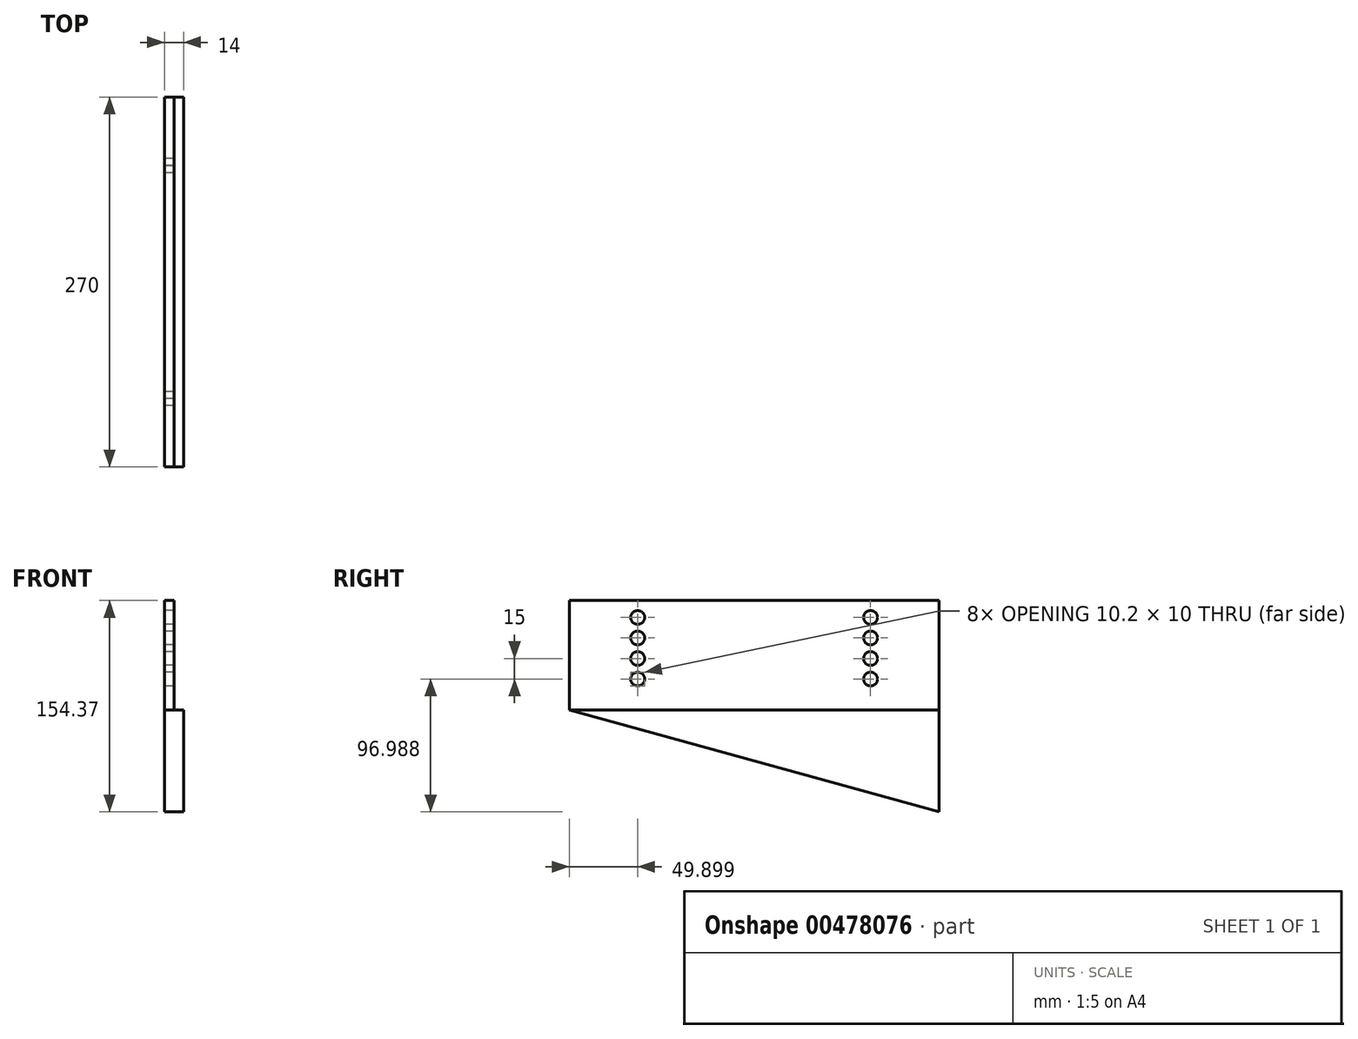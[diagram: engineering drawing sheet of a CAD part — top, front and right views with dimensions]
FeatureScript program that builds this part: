
annotation { "Feature Type Name" : "Feature", "Feature Type Description" : "" }
export const myFeature = defineFeature(function(context is Context, id is Id, definition is map)
    precondition{}
    {
        {
            var Q0;
            Q0=qCreatedBy(makeId("Right.planeOp"),FACE);
            var sketch = newSketch(context, id + "F0", { "sketchPlane" : qUnion([Q0])});
            skLineSegment(sketch, "E0", {"start": v(-152.41, 80) * mm, "end": v(117.59, 80) * mm});
            skLineSegment(sketch, "E1", {"start": v(117.59, -74.37) * mm, "end": v(117.59, 80) * mm});
            skLineSegment(sketch, "E2", {"start": v(-102.41, 80) * mm, "end": v(67.59, 80) * mm});
            skLineSegment(sketch, "E3", {"start": v(117.59, -74.37) * mm, "end": v(-152.41, 0) * mm});
            skLineSegment(sketch, "E4", {"start": v(117.59, 0) * mm, "end": v(-152.41, 0) * mm});
            skLineSegment(sketch, "E5", {"start": v(-152.41, 80) * mm, "end": v(-152.41, 0) * mm});
            skCircle(sketch, "E6", {"center": v(-102.41, 67.62) * mm, "radius": 5 * mm});
            skCircle(sketch, "E7", {"center": v(67.59, 67.62) * mm, "radius": 5 * mm});
            skCircle(sketch, "E8.0.1.0", {"center": v(67.59, 52.62) * mm, "radius": 5 * mm});
            skCircle(sketch, "E8.0.1.1", {"center": v(-102.41, 52.62) * mm, "radius": 5 * mm});
            skCircle(sketch, "E8.0.2.0", {"center": v(67.59, 37.62) * mm, "radius": 5 * mm});
            skCircle(sketch, "E8.0.2.1", {"center": v(-102.41, 37.62) * mm, "radius": 5 * mm});
            skCircle(sketch, "E8.0.3.0", {"center": v(67.59, 22.62) * mm, "radius": 5 * mm});
            skCircle(sketch, "E8.0.3.1", {"center": v(-102.41, 22.62) * mm, "radius": 5 * mm});
            skCircle(sketch, "E8.1.0.0", {"center": v(67.49, 67.62) * mm, "radius": 5 * mm});
            skCircle(sketch, "E8.1.0.1", {"center": v(-102.51, 67.62) * mm, "radius": 5 * mm});
            skCircle(sketch, "E8.1.1.0", {"center": v(67.49, 52.62) * mm, "radius": 5 * mm});
            skCircle(sketch, "E8.1.1.1", {"center": v(-102.51, 52.62) * mm, "radius": 5 * mm});
            skCircle(sketch, "E8.1.2.0", {"center": v(67.49, 37.62) * mm, "radius": 5 * mm});
            skCircle(sketch, "E8.1.2.1", {"center": v(-102.51, 37.62) * mm, "radius": 5 * mm});
            skCircle(sketch, "E8.1.3.0", {"center": v(67.49, 22.62) * mm, "radius": 5 * mm});
            skCircle(sketch, "E8.1.3.1", {"center": v(-102.51, 22.62) * mm, "radius": 5 * mm});
            skCircle(sketch, "E8.2.0.0", {"center": v(67.39, 67.62) * mm, "radius": 5 * mm});
            skCircle(sketch, "E8.2.0.1", {"center": v(-102.61, 67.62) * mm, "radius": 5 * mm});
            skCircle(sketch, "E8.2.1.0", {"center": v(67.39, 52.62) * mm, "radius": 5 * mm});
            skCircle(sketch, "E8.2.1.1", {"center": v(-102.61, 52.62) * mm, "radius": 5 * mm});
            skCircle(sketch, "E8.2.2.0", {"center": v(67.39, 37.62) * mm, "radius": 5 * mm});
            skCircle(sketch, "E8.2.2.1", {"center": v(-102.61, 37.62) * mm, "radius": 5 * mm});
            skCircle(sketch, "E8.2.3.0", {"center": v(67.39, 22.62) * mm, "radius": 5 * mm});
            skCircle(sketch, "E8.2.3.1", {"center": v(-102.61, 22.62) * mm, "radius": 5 * mm});
            skLineSegment(sketch, "E8.direction1", {"start": v(67.59, 67.62) * mm, "end": v(67.49, 67.62) * mm, "construction": true});
            skLineSegment(sketch, "E8.direction2", {"start": v(67.59, 67.62) * mm, "end": v(67.59, 52.62) * mm, "construction": true});
            skSolve(sketch);
        }
        {
            var Q0;
            {var subQ0=sQuery(id+"F0.wireOp",EDGE,"E5");Q0=makeQuery(id+"F0.imprint","IMPRINT",FACE,{"disambiguationData":[TD([[makeQuery(id+"F0.imprint","IMPRINT",EDGE,{"derivedFrom":subQ0}),1.0]])]});}
            var Q1;
            {var subQ5=sQuery(id+"F0.wireOp",EDGE,"kZBZgwTT-XFhY-glHP-XGmq-IiVmHmRIZegb");var subQ6=sQuery(id+"F0.wireOp",EDGE,"E4");var subQ7=makeQuery(id+"F0.imprint","INTERSECT",VERTEX,{"derivedFrom":[subQ6,subQ5]});Q1=makeQuery(id+"F0.imprint","IMPRINT",FACE,{"disambiguationData":[TD([[makeQuery(id+"F0.imprint","IMPRINT",EDGE,{"disambiguationData":[TD([[subQ7,1.0]])],"derivedFrom":subQ6}),-1.0]])]});}
            var Q2;
            {var subQ1=sQuery(id+"F0.wireOp",EDGE,"E2");Q2=makeQuery(id+"F0.imprint","IMPRINT",FACE,{"disambiguationData":[TD([[makeQuery(id+"F0.imprint","IMPRINT",EDGE,{"derivedFrom":subQ1}),-1.0]])]});}
            var Q3;
            {var subQ1=sQuery(id+"F0.wireOp",EDGE,"E0");var subQ5=sQuery(id+"F0.wireOp",EDGE,"E1");var subQ6=makeQuery(id+"F0.imprint","INTERSECT",VERTEX,{"derivedFrom":[subQ1,subQ5]});Q3=makeQuery(id+"F0.imprint","IMPRINT",FACE,{"disambiguationData":[TD([[makeQuery(id+"F0.imprint","IMPRINT",EDGE,{"disambiguationData":[TD([[subQ6,1.0]])],"derivedFrom":subQ5}),1.0]])]});}
            var Q4;
            {var subQ4=sQuery(id+"F0.wireOp",EDGE,"E3");Q4=makeQuery(id+"F0.imprint","IMPRINT",FACE,{"disambiguationData":[TD([[makeQuery(id+"F0.imprint","IMPRINT",EDGE,{"derivedFrom":subQ4}),-1.0]])]});}
            extrude(context, id + "F1", {"entities" : qUnion([Q0, Q1, Q2, Q3, Q4]), "depth" : 7 * mm});
        }
        {
            var Q0;
            Q0=makeQuery(id+"F1.opExtrude","CAP_FACE",FACE,{"disambiguationData":[OSD([sQuery(id+"F0.wireOp",EDGE,"E0"),sQuery(id+"F0.wireOp",EDGE,"E1"),sQuery(id+"F0.wireOp",EDGE,"E2"),sQuery(id+"F0.wireOp",EDGE,"E3"),sQuery(id+"F0.wireOp",EDGE,"E5"),sQuery(id+"F0.wireOp",EDGE,"E6"),sQuery(id+"F0.wireOp",EDGE,"E7")])],"isStart":true});
            var sketch = newSketch(context, id + "F2", { "sketchPlane" : qUnion([Q0])});
            skLineSegment(sketch, "E9", {"start": v(152.41, 0) * mm, "end": v(-117.59, 0) * mm});
            skLineSegment(sketch, "E10", {"start": v(-117.59, 0) * mm, "end": v(-117.59, -74.37) * mm});
            skLineSegment(sketch, "E11", {"start": v(-117.59, -74.37) * mm, "end": v(152.41, 0) * mm});
            skSolve(sketch);
        }
        {
            var Q0;
            Q0=makeQuery(id+"F2.imprint","IMPRINT",FACE,{"disambiguationData":[TD([[makeQuery(id+"F2.imprint","IMPRINT",EDGE,{"derivedFrom":sQuery(id+"F2.wireOp",EDGE,"E9")}),1.0]])]});
            extrude(context, id + "F3", {"entities" : qUnion([Q0]), "operationType" : NewBodyOperationType.ADD, "oppositeDirection" : true, "depth" : 14 * mm});
        }
    });
